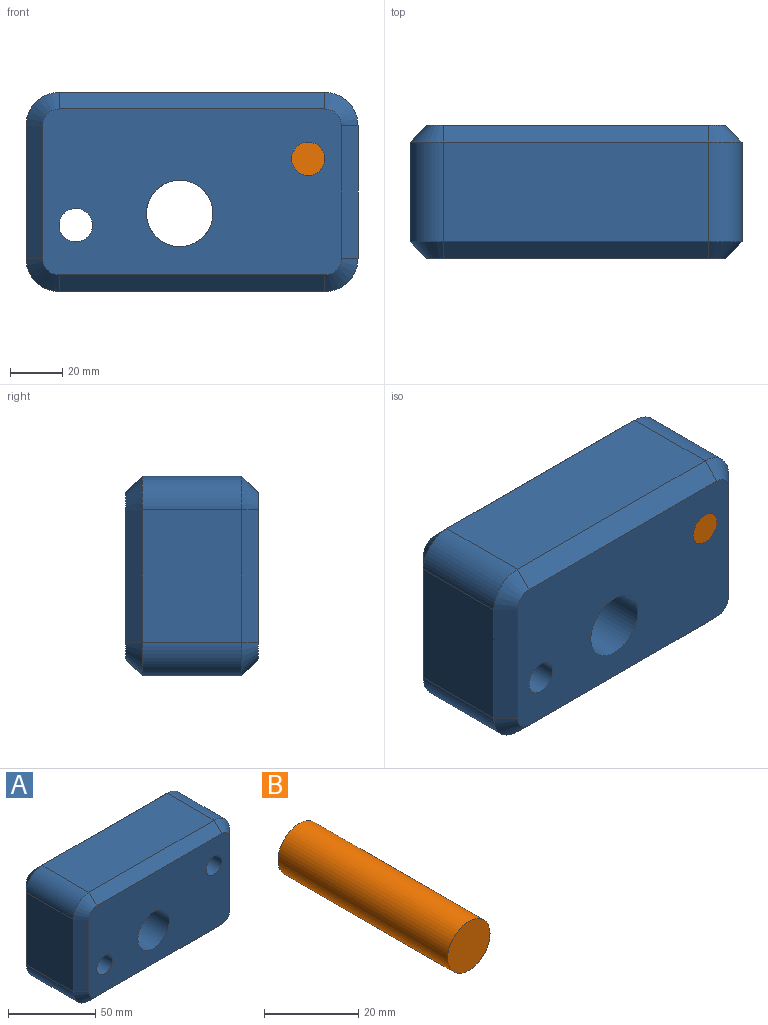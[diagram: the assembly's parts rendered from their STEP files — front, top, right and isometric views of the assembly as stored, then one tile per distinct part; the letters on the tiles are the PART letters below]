
ASSEMBLY  parts=2 mates=1
PART A: 29 faces, bbox 127x50.8x76.2 mm
  f0: plane 50.8x38.1mm, normal (-1,0,0), area 1935.5mm2, adj f9,f12,f16,f24
  f1: plane 101.6x38.1mm, normal (0,0,-1), area 3871mm2, adj f11,f12,f20,f28
  f2: plane 50.8x38.1mm, normal (1,0,0), area 1935.5mm2, adj f10,f11,f17,f25
  f3: cylinder r=6.35mm len=50.8mm, axis (0,1,0), area 2026.8mm2, adj f6,f7
  f4: cylinder r=6.35mm len=50.8mm, axis (0,1,0), area 2026.8mm2, adj f6,f7
  f5: plane 101.6x38.1mm, normal (0,0,1), area 3871mm2, adj f9,f10,f13,f21
  f6: plane 114.3x63.5mm, normal (0,-1,0), area 6463.4mm2, adj f3,f4,f8,f21,f22,f23,f24,f25
  f7: plane 114.3x63.5mm, normal (0,1,0), area 6463.4mm2, adj f3,f4,f8,f13,f14,f15,f16,f17
  f8: cylinder r=12.7mm len=50.8mm, axis (0,-1,0), area 4053.7mm2, adj f6,f7
  f9: cylinder r=12.7mm len=38.1mm, axis (0,-1,0), area 760.1mm2, adj f0,f5,f14,f22
  f10: cylinder r=12.7mm len=38.1mm, axis (0,1,0), area 760.1mm2, adj f2,f5,f15,f23
  f11: cylinder r=12.7mm len=38.1mm, axis (0,-1,0), area 760.1mm2, adj f1,f2,f19,f27
  f12: cylinder r=12.7mm len=38.1mm, axis (0,1,0), area 760.1mm2, adj f0,f1,f18,f26
  f13: plane 101.6x6.35mm, normal (0,0.71,0.71), area 912.4mm2, adj f5,f7,f14,f15
  f14: cone r=6.35mm half-angle=45deg, axis (0,-1,0), area 134.4mm2, adj f7,f9,f13,f16
  f15: cone r=6.35mm half-angle=45deg, axis (0,-1,0), area 134.4mm2, adj f7,f10,f13,f17
  f16: plane 50.8x6.35mm, normal (-0.71,0.71,0), area 456.2mm2, adj f0,f7,f14,f18
  f17: plane 50.8x6.35mm, normal (0.71,0.71,0), area 456.2mm2, adj f2,f7,f15,f19
  f18: cone r=6.35mm half-angle=45deg, axis (0,-1,0), area 134.4mm2, adj f7,f12,f16,f20
  f19: cone r=6.35mm half-angle=45deg, axis (0,-1,0), area 134.4mm2, adj f7,f11,f17,f20
  f20: plane 101.6x6.35mm, normal (0,0.71,-0.71), area 912.4mm2, adj f1,f7,f18,f19
  f21: plane 101.6x6.35mm, normal (0,-0.71,0.71), area 912.4mm2, adj f5,f6,f22,f23
  f22: cone r=6.35mm half-angle=45deg, axis (0,1,0), area 134.4mm2, adj f6,f9,f21,f24
  f23: cone r=6.35mm half-angle=45deg, axis (0,1,0), area 134.4mm2, adj f6,f10,f21,f25
  f24: plane 50.8x6.35mm, normal (-0.71,-0.71,0), area 456.2mm2, adj f0,f6,f22,f26
  f25: plane 50.8x6.35mm, normal (0.71,-0.71,0), area 456.2mm2, adj f2,f6,f23,f27
  f26: cone r=6.35mm half-angle=45deg, axis (0,1,0), area 134.4mm2, adj f6,f12,f24,f28
  f27: cone r=6.35mm half-angle=45deg, axis (0,1,0), area 134.4mm2, adj f6,f11,f25,f28
  f28: plane 101.6x6.35mm, normal (0,-0.71,-0.71), area 912.4mm2, adj f1,f6,f26,f27
PART B: 3 faces, bbox 12.7x50.8x12.7 mm
  f0: cylinder r=6.35mm len=50.8mm, axis (0,1,0), area 2026.8mm2, adj f1,f2
  f1: plane 12.7x12.7mm, normal (0,-1,0), area 126.7mm2, adj f0
  f2: plane 12.7x12.7mm, normal (0,1,0), area 126.7mm2, adj f0
PLACE A t=(-19.52,4.6,-7.23)mm fixed
PLACE B t=(70.4,4.6,-38.2)mm
MATE cylindrical B.f0 <-> A.f3  axis (0,1,0) through (23.69,4.6,-0.52)mm
